# Revit family: Access Chambers - 550,700,900(Shrd)
name_source: partatom
category: Plumbing Fixtures
revit_build: Autodesk Revit 2013 (Build: 20120221_2030(x64)
units: mm (PartAtom-declared; Revit-internal decimal feet)

## types (4) — shared parameters
ACO Hydraulic Design Software = http://www.acodesign.co.uk
Access Chamber Colour = Black
Access Chamber Material = Medium Density Polyethylene
Access Chamber Recyclable = Fully recyclable
Access Chamber Recycled Material Content = Variable %
Assembly Code = D2040
Coarse_Chamber_Depth = -1500 mm  [stored -4.92126 ft]
Coarse_Cover_Depth = -150 mm
Cover & Frame Finish = Water Based Paint Coating
Cover & Frame Material = Ductile Iron
Cover & Frame Recyclable = Fully recyclable
Cover & Frame Recycled Material Content = Between 40% - 90%
Depth Overall = 1500
Floor Opening Width = 621 mm  [stored 2.0374 ft]
Installation - Reinforcement Details = Refer to brochure
Installation guidelines = http://www.aco.co.uk
Maintenance guidelines = http://www.aco.co.uk
Manufacturer = ACO Technologies plc - ACO Water Management Division
Model = ACO Qmax 550 700 900 Access and Silt Chambers
Model Description = High capacity slot drainage channel system
Price = POA - contact ACO
Product Dimensions = 870mm x 800mm x 1500mm (LxWxH)
Product Page URL = http://www.aco.co.uk
Product Standard = BS EN 124:1994 CE  marked
Product brochure = http://www.aco.co.uk
Revision = 1
SerialNumber = 0.000000
TagNumber = 0.000000
Telephone = +44 (0)1462 816666
Top of Access-IO-Silt = -150 mm
URL = www.aco.co.uk
Width Overall = 870 mm  [stored 2.85433 ft]
zero-valued in all types: Cost

## per-type parameters (varying)
| type | Cover & Frame Colour | Drainage Slot Intake area | Drainage Slot Width | Fax | Installation - Concrete Grade | Load Class | Product Weight | Type Comments | V_Slotted Cover | V_Solid Cover |
| 44314 | Black | 120182mm² | 21mm | +44 (0)1462 815895 | Refer to brochure | A 15 - D 400 | 148 kg | ACO Qmax 550 700 900 Access Chamber with D 400 Slotted Cover & Frame | Yes | No |
| 44315 | Black
Black |  |  | +44 (0)1462 815895 | Refer to brochure | A 15 - D 400 | 147 kg | ACO Qmax 550 700 900 Access Chamber with D 400 Solid Cover & Frame | No | Yes |
| 44316 | Black | 120182mm² | 21mm | +44 (0)1462 815895 | Refer to brochure | A 15 - F 900 | 181 kg | ACO Qmax 550 700 900 Access Chamber with F 900 Slotted Cover & Frame | Yes | No |
| 44317 | Black |  |  | +44 (0)1462 815895
+44 (0)1462 815895 | Refer to brochure
Refer to brochure | A 15 - F 900 | 175 kg | ACO Qmax 550 700 900 Access Chamber with F 900 Solid Cover & Frame | No | Yes |

note: column(s) folded — value = type name in every type: Product Code

note: [stored X ft] marks values corroborated as IEEE doubles in the binary element streams (Revit-internal decimal feet)

## geometry (parser evidence)
native form markers: Blend x2, Sweep x3
no freeform markers — native parametric forms only
